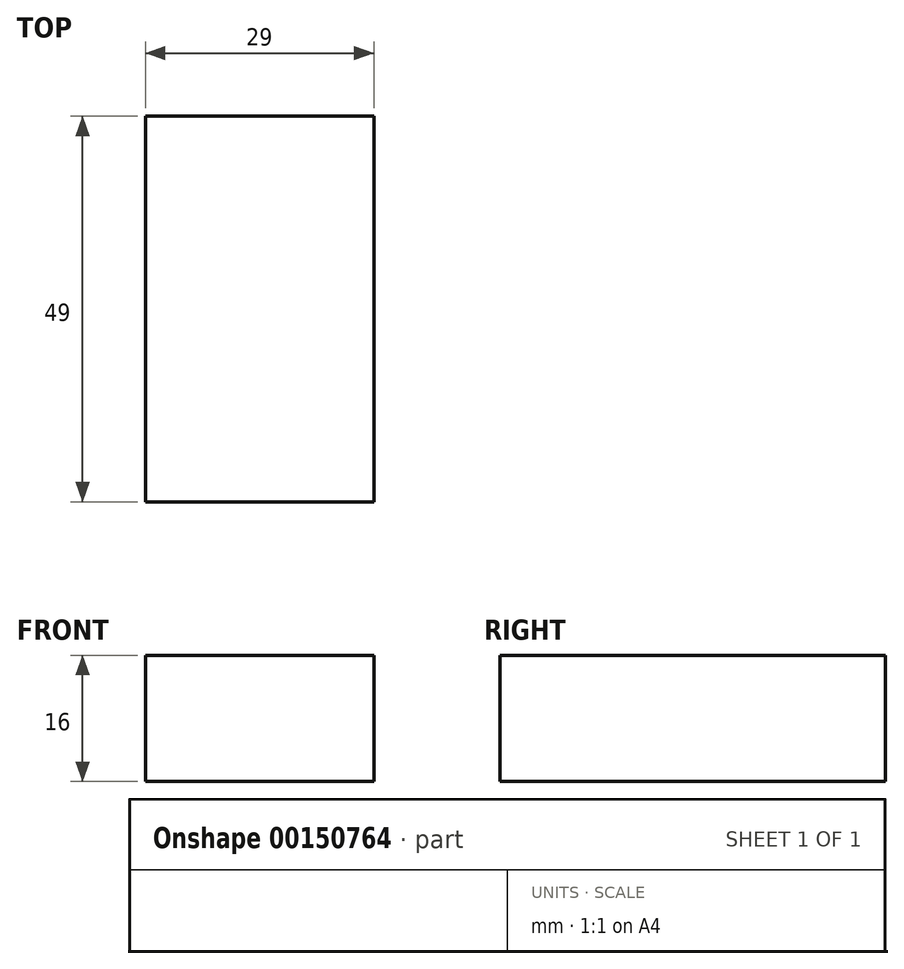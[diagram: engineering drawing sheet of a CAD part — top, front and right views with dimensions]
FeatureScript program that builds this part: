
annotation { "Feature Type Name" : "Feature", "Feature Type Description" : "" }
export const myFeature = defineFeature(function(context is Context, id is Id, definition is map)
    precondition{}
    {
        {
            var Q0;
            Q0=qCreatedBy(makeId("Top.planeOp"),FACE);
            var sketch = newSketch(context, id + "F0", { "sketchPlane" : qUnion([Q0])});
            skLineSegment(sketch, "E0.bottom", {"start": v(-14.5, 24.5) * mm, "end": v(14.5, 24.5) * mm});
            skLineSegment(sketch, "E0.top", {"start": v(-14.5, -24.5) * mm, "end": v(14.5, -24.5) * mm});
            skLineSegment(sketch, "E0.left", {"start": v(-14.5, 24.5) * mm, "end": v(-14.5, -24.5) * mm});
            skLineSegment(sketch, "E0.right", {"start": v(14.5, 24.5) * mm, "end": v(14.5, -24.5) * mm});
            skPoint(sketch, "E0.middle", {"position": v(0, 0) * mm});
            skSolve(sketch);
        }
        {
            var Q0;
            Q0 = qSketchRegion(id + "F0", true);
            extrude(context, id + "F1", {"entities" : qUnion([Q0]), "depth" : 16 * mm});
        }
    });
